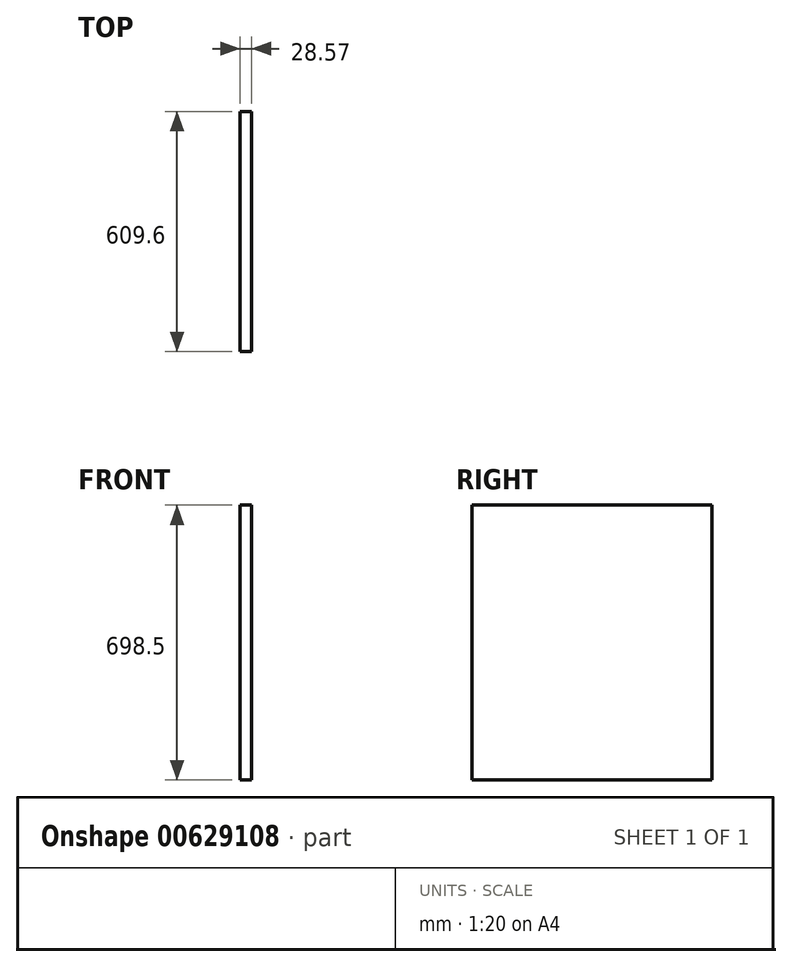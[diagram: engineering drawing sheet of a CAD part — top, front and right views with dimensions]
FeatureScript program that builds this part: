
annotation { "Feature Type Name" : "Feature", "Feature Type Description" : "" }
export const myFeature = defineFeature(function(context is Context, id is Id, definition is map)
    precondition{}
    {
        {
            var Q0;
            Q0=qCreatedBy(makeId("Right.planeOp"),FACE);
            var sketch = newSketch(context, id + "F0", { "sketchPlane" : qUnion([Q0])});
            skLineSegment(sketch, "E0.bottom", {"start": v(304.8, 349.25) * mm, "end": v(-304.8, 349.25) * mm});
            skLineSegment(sketch, "E0.top", {"start": v(304.8, -349.25) * mm, "end": v(-304.8, -349.25) * mm});
            skLineSegment(sketch, "E0.left", {"start": v(304.8, 349.25) * mm, "end": v(304.8, -349.25) * mm});
            skLineSegment(sketch, "E0.right", {"start": v(-304.8, 349.25) * mm, "end": v(-304.8, -349.25) * mm});
            skPoint(sketch, "E0.middle", {"position": v(0, 0) * mm});
            skSolve(sketch);
        }
        {
            var Q0;
            Q0=makeQuery(id+"F0.imprint","IMPRINT",FACE,{"disambiguationData":[TD([[makeQuery(id+"F0.imprint","IMPRINT",EDGE,{"derivedFrom":sQuery(id+"F0.wireOp",EDGE,"E0.bottom")}),1.0]])]});
            extrude(context, id + "F1", {"entities" : qUnion([Q0]), "depth" : 28.57 * mm, "offsetDistance" : 25.4 * mm});
        }
    });
